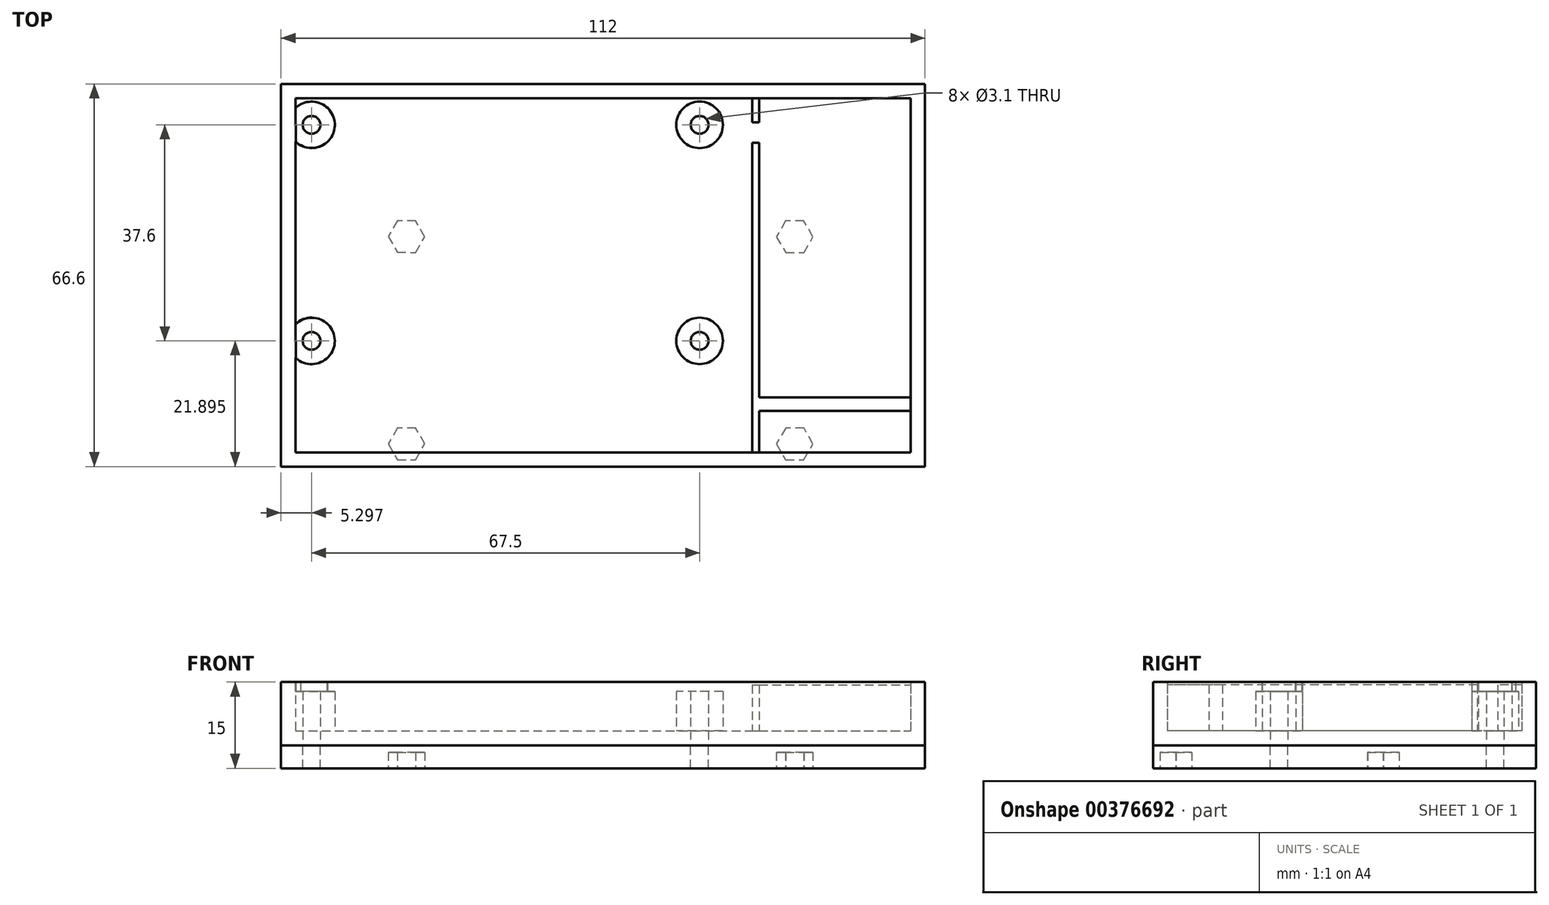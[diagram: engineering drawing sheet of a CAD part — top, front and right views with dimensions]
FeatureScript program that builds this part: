
annotation { "Feature Type Name" : "Feature", "Feature Type Description" : "" }
export const myFeature = defineFeature(function(context is Context, id is Id, definition is map)
    precondition{}
    {
        {
            var Q0;
            Q0=qCreatedBy(makeId("Top.planeOp"),FACE);
            var sketch = newSketch(context, id + "F0", { "sketchPlane" : qUnion([Q0])});
            skLineSegment(sketch, "E0.bottom", {"start": v(-67.04, 57.24) * mm, "end": v(44.96, 57.24) * mm});
            skLineSegment(sketch, "E0.top", {"start": v(-67.04, -9.36) * mm, "end": v(-25.04, -9.36) * mm});
            skLineSegment(sketch, "E0.left", {"start": v(-67.04, 57.24) * mm, "end": v(-67.04, -9.36) * mm});
            skLineSegment(sketch, "E0.right", {"start": v(44.96, 57.24) * mm, "end": v(44.96, -9.36) * mm});
            skLineSegment(sketch, "E1", {"start": v(44.63, 50.14) * mm, "end": v(176.63, 50.14) * mm, "construction": true});
            skLineSegment(sketch, "E2", {"start": v(42, 12.54) * mm, "end": v(176.63, 12.54) * mm, "construction": true});
            skLineSegment(sketch, "E3", {"start": v(-61.74, -1.53) * mm, "end": v(-61.74, -83.47) * mm, "construction": true});
            skLineSegment(sketch, "E4", {"start": v(5.76, -0.22) * mm, "end": v(5.76, -80.28) * mm, "construction": true});
            skLineSegment(sketch, "E5", {"start": v(1.1, -53.47) * mm, "end": v(1.1, -86.28) * mm, "construction": true});
            skLineSegment(sketch, "E6", {"start": v(38.82, -0.26) * mm, "end": v(130.32, -0.26) * mm, "construction": true});
            skCircle(sketch, "E7", {"center": v(-61.74, 50.14) * mm, "radius": 1.55 * mm});
            skCircle(sketch, "E8", {"center": v(5.76, 50.14) * mm, "radius": 1.55 * mm});
            skCircle(sketch, "E9", {"center": v(-61.74, 12.54) * mm, "radius": 1.55 * mm});
            skCircle(sketch, "E10", {"center": v(5.76, 12.54) * mm, "radius": 1.55 * mm});
            skLineSegment(sketch, "E11", {"start": v(-13.54, -55.9) * mm, "end": v(-13.54, -82.43) * mm, "construction": true});
            skLineSegment(sketch, "E12.trimOffspring", {"start": v(-13.54, -9.36) * mm, "end": v(44.96, -9.36) * mm});
            skLineSegment(sketch, "E13", {"start": v(-25.04, -9.36) * mm, "end": v(-13.54, -9.36) * mm});
            skSolve(sketch);
        }
        {
            var Q0;
            Q0 = qSketchRegion(id + "F0", true);
            var Q1;
            {var subQ0=sQuery(id+"F0.wireOp",EDGE,"FsC10DJD-oyt9-5rBi-kH7v-Q8Pfx3An0YuG");Q1=makeQuery(id+"F0.imprint","IMPRINT",FACE,{"disambiguationData":[TD([[makeQuery(id+"F0.imprint","IMPRINT",EDGE,{"derivedFrom":subQ0}),-1.0]])]});}
            extrude(context, id + "F1", {"entities" : qUnion([Q0, Q1]), "oppositeDirection" : true, "depth" : 4 * mm});
        }
        {
            var Q0;
            Q0=makeQuery(id+"F0.imprint","IMPRINT",FACE,{"disambiguationData":[TD([[makeQuery(id+"F0.imprint","IMPRINT",EDGE,{"derivedFrom":sQuery(id+"F0.wireOp",EDGE,"E0.bottom")}),-1.0]])]});
            extrude(context, id + "F2", {"entities" : qUnion([Q0]), "depth" : 11 * mm});
        }
        {
            var Q0;
            Q0=makeQuery(id+"F2.opExtrude","CAP_FACE",FACE,{"disambiguationData":[OSD([sQuery(id+"F0.wireOp",EDGE,"E0.bottom"),sQuery(id+"F0.wireOp",EDGE,"E0.top"),sQuery(id+"F0.wireOp",EDGE,"E0.left"),sQuery(id+"F0.wireOp",EDGE,"E0.right"),sQuery(id+"F0.wireOp",EDGE,"E7"),sQuery(id+"F0.wireOp",EDGE,"E8"),sQuery(id+"F0.wireOp",EDGE,"E9"),sQuery(id+"F0.wireOp",EDGE,"E10"),sQuery(id+"F0.wireOp",EDGE,"E12.trimOffspring"),sQuery(id+"F0.wireOp",EDGE,"E13")])],"isStart":false});
            shell(context, id + "F3", {"entities" : qUnion([Q0]), "thickness" : 2.5 * mm});
        }
        {
            var Q0;
            {var subQ0=sQuery(id+"F0.wireOp",EDGE,"E13");var subQ1=sQuery(id+"F0.wireOp",EDGE,"E12.trimOffspring");var subQ2=sQuery(id+"F0.wireOp",EDGE,"E10");var subQ3=sQuery(id+"F0.wireOp",EDGE,"E9");var subQ4=sQuery(id+"F0.wireOp",EDGE,"E8");var subQ5=sQuery(id+"F0.wireOp",EDGE,"E7");var subQ6=sQuery(id+"F0.wireOp",EDGE,"E0.right");var subQ7=sQuery(id+"F0.wireOp",EDGE,"E0.left");var subQ8=sQuery(id+"F0.wireOp",EDGE,"E0.top");var subQ9=sQuery(id+"F0.wireOp",EDGE,"E0.bottom");Q0=makeQuery(id+"F3.opShell","OFFSET_FACE",FACE,{"disambiguationData":[OSD([subQ9,subQ8,subQ7,subQ6,subQ5,subQ4,subQ3,subQ2,subQ1,subQ0]),TDD([makeQuery(id+"F2.opExtrude","CAP_FACE",FACE,{"disambiguationData":[OSD([subQ9,subQ8,subQ7,subQ6,subQ5,subQ4,subQ3,subQ2,subQ1,subQ0])],"isStart":true})])]});}
            cPlane(context, id + "F4", {"entities" : qUnion([Q0]), "cplaneType" : CPlaneType.OFFSET, "offset" : 0 * mm, "width" : 150 * mm, "height" : 150 * mm});
        }
        {
            var Q0;
            Q0=qCreatedBy(id+"F4.planeOp",FACE);
            var sketch = newSketch(context, id + "F5", { "sketchPlane" : qUnion([Q0])});
            skLineSegment(sketch, "E14.bottom", {"start": v(14.9, 54.77) * mm, "end": v(16.11, 54.77) * mm});
            skLineSegment(sketch, "E14.top", {"start": v(14.9, 50.6) * mm, "end": v(16.11, 50.6) * mm});
            skLineSegment(sketch, "E14.left", {"start": v(14.9, 54.77) * mm, "end": v(14.9, 50.6) * mm});
            skLineSegment(sketch, "E14.right", {"start": v(16.11, 54.77) * mm, "end": v(16.11, 50.6) * mm});
            skLineSegment(sketch, "E15.bottom", {"start": v(14.92, 47.04) * mm, "end": v(16.11, 47.04) * mm});
            skLineSegment(sketch, "E15.top", {"start": v(14.92, -6.86) * mm, "end": v(16.11, -6.86) * mm});
            skLineSegment(sketch, "E15.left", {"start": v(14.92, 47.04) * mm, "end": v(14.92, -6.86) * mm});
            skLineSegment(sketch, "E15.right", {"start": v(16.11, 47.04) * mm, "end": v(16.11, -6.86) * mm});
            skLineSegment(sketch, "E16.bottom", {"start": v(16.11, 2.7) * mm, "end": v(42.48, 2.7) * mm});
            skLineSegment(sketch, "E16.top", {"start": v(16.11, 0.35) * mm, "end": v(42.48, 0.35) * mm});
            skLineSegment(sketch, "E16.left", {"start": v(16.11, 2.7) * mm, "end": v(16.11, 0.35) * mm});
            skLineSegment(sketch, "E16.right", {"start": v(42.48, 2.7) * mm, "end": v(42.48, 0.35) * mm});
            skSolve(sketch);
        }
        {
            var Q0;
            Q0=makeQuery(id+"F5.imprint","IMPRINT",FACE,{"disambiguationData":[TD([[makeQuery(id+"F5.imprint","IMPRINT",EDGE,{"derivedFrom":sQuery(id+"F5.wireOp",EDGE,"E14.bottom")}),-1.0]])]});
            var Q1;
            {var subQ1=sQuery(id+"F5.wireOp",EDGE,"E15.bottom");Q1=makeQuery(id+"F5.imprint","IMPRINT",FACE,{"disambiguationData":[TD([[makeQuery(id+"F5.imprint","IMPRINT",EDGE,{"derivedFrom":subQ1}),-1.0]])]});}
            var Q2;
            Q2=makeQuery(id+"F5.imprint","IMPRINT",FACE,{"disambiguationData":[TD([[makeQuery(id+"F5.imprint","IMPRINT",EDGE,{"derivedFrom":sQuery(id+"F5.wireOp",EDGE,"E16.bottom")}),-1.0]])]});
            extrude(context, id + "F6", {"entities" : qUnion([Q0, Q1, Q2]), "depth" : 8 * mm});
        }
        {
            var Q0;
            Q0=makeQuery(id+"F2.opExtrude","CAP_FACE",FACE,{"disambiguationData":[OSD([sQuery(id+"F0.wireOp",EDGE,"A0NuOWqy-mbow-oFeQ-aFUs-JcpJWNl4cWgZ.bottom"),sQuery(id+"F0.wireOp",EDGE,"A0NuOWqy-mbow-oFeQ-aFUs-JcpJWNl4cWgZ.top"),sQuery(id+"F0.wireOp",EDGE,"A0NuOWqy-mbow-oFeQ-aFUs-JcpJWNl4cWgZ.left"),sQuery(id+"F0.wireOp",EDGE,"A0NuOWqy-mbow-oFeQ-aFUs-JcpJWNl4cWgZ.right"),sQuery(id+"F0.wireOp",EDGE,"l8DgdMRk-jwTu-yn87-Ubay-0boQf5sXXbED"),sQuery(id+"F0.wireOp",EDGE,"IFopZNKl-To2k-V7rv-e193-DWKehgoEgPML"),sQuery(id+"F0.wireOp",EDGE,"wSwp0tQP-pvOi-1nlV-F12w-8n0LTa4ZxAE6"),sQuery(id+"F0.wireOp",EDGE,"Evtd0GlZ-4YtB-NOmt-JUBp-SgV2YzHuL3n0"),sQuery(id+"F0.wireOp",EDGE,"269334cf-922f-445a-855f-7391bd0f7049.trimOffspring"),sQuery(id+"F0.wireOp",EDGE,"TvPx72jC-Pm7q-U3J5-DLNJ-bXEKM7csz5V9"),sQuery(id+"F0.wireOp",EDGE,"zx5NMsNx-JtPk-FpRE-2ajY-Q3JxvkHSanLY"),sQuery(id+"F0.wireOp",EDGE,"5lGAd6N5-jAS0-xnDL-4Krg-xO5UTL4uwT4z"),sQuery(id+"F0.wireOp",EDGE,"S9dVnHw2-FrOM-Ck64-E3qb-46jiesPe1zGM")])],"isStart":false});
            var Q1;
            {var subQ0=sQuery(id+"F0.wireOp",EDGE,"E13");var subQ1=sQuery(id+"F0.wireOp",EDGE,"E12.trimOffspring");var subQ2=sQuery(id+"F0.wireOp",EDGE,"E10");var subQ3=sQuery(id+"F0.wireOp",EDGE,"E9");var subQ4=sQuery(id+"F0.wireOp",EDGE,"E8");var subQ5=sQuery(id+"F0.wireOp",EDGE,"E7");var subQ6=sQuery(id+"F0.wireOp",EDGE,"E0.right");var subQ7=sQuery(id+"F0.wireOp",EDGE,"E0.left");var subQ8=sQuery(id+"F0.wireOp",EDGE,"E0.top");var subQ9=sQuery(id+"F0.wireOp",EDGE,"E0.bottom");Q1=makeQuery(id+"F3.opShell","OFFSET_FACE",FACE,{"disambiguationData":[OSD([subQ9,subQ8,subQ7,subQ6,subQ5,subQ4,subQ3,subQ2,subQ1,subQ0]),TDD([makeQuery(id+"F2.opExtrude","CAP_FACE",FACE,{"disambiguationData":[OSD([subQ9,subQ8,subQ7,subQ6,subQ5,subQ4,subQ3,subQ2,subQ1,subQ0])],"isStart":false})]),OD(1.0)]});}
            cPlane(context, id + "F7", {"entities" : qUnion([Q0, Q1]), "cplaneType" : CPlaneType.OFFSET, "offset" : 0 * mm, "width" : 150 * mm, "height" : 150 * mm});
        }
        {
            var Q0;
            Q0=qCreatedBy(id+"F7.planeOp",FACE);
            var sketch = newSketch(context, id + "F8", { "sketchPlane" : qUnion([Q0])});
            skArc(sketch, "E17", {"start": v(-64.48, 47.2) * mm, "mid": v(-57.67, 50.2) * mm, "end": v(-64.53, 53.06) * mm});
            skLineSegment(sketch, "E18", {"start": v(-64.53, 53.06) * mm, "end": v(-64.48, 47.2) * mm});
            skArc(sketch, "E19", {"start": v(-64.48, 9.53) * mm, "mid": v(-57.66, 12.55) * mm, "end": v(-64.55, 15.4) * mm});
            skLineSegment(sketch, "E20", {"start": v(-64.55, 15.4) * mm, "end": v(-64.48, 9.53) * mm});
            skCircle(sketch, "E21", {"center": v(5.75, 50.14) * mm, "radius": 4.24 * mm});
            skCircle(sketch, "E22", {"center": v(5.75, 12.54) * mm, "radius": 4.31 * mm});
            skSolve(sketch);
        }
        {
            var Q0;
            Q0=makeQuery(id+"F8.imprint","IMPRINT",FACE,{"disambiguationData":[TD([[makeQuery(id+"F8.imprint","IMPRINT",EDGE,{"derivedFrom":sQuery(id+"F8.wireOp",EDGE,"E21")}),1.0]])]});
            var Q1;
            Q1=makeQuery(id+"F8.imprint","IMPRINT",FACE,{"disambiguationData":[TD([[makeQuery(id+"F8.imprint","IMPRINT",EDGE,{"derivedFrom":sQuery(id+"F8.wireOp",EDGE,"E22")}),1.0]])]});
            var Q2;
            Q2=makeQuery(id+"F8.imprint","IMPRINT",FACE,{"disambiguationData":[TD([[makeQuery(id+"F8.imprint","IMPRINT",EDGE,{"derivedFrom":sQuery(id+"F8.wireOp",EDGE,"E17")}),1.0]])]});
            var Q3;
            Q3=makeQuery(id+"F8.imprint","IMPRINT",FACE,{"disambiguationData":[TD([[makeQuery(id+"F8.imprint","IMPRINT",EDGE,{"derivedFrom":sQuery(id+"F8.wireOp",EDGE,"E19")}),1.0]])]});
            extrude(context, id + "F9", {"entities" : qUnion([Q0, Q1, Q2, Q3]), "operationType" : NewBodyOperationType.REMOVE, "oppositeDirection" : true, "depth" : 1.62 * mm});
        }
        {
            var Q0;
            Q0=makeQuery(id+"F1.opExtrude","CAP_FACE",FACE,{"disambiguationData":[OSD([sQuery(id+"F0.wireOp",EDGE,"E0.bottom"),sQuery(id+"F0.wireOp",EDGE,"E0.top"),sQuery(id+"F0.wireOp",EDGE,"E0.left"),sQuery(id+"F0.wireOp",EDGE,"E0.right"),sQuery(id+"F0.wireOp",EDGE,"E7"),sQuery(id+"F0.wireOp",EDGE,"E8"),sQuery(id+"F0.wireOp",EDGE,"E9"),sQuery(id+"F0.wireOp",EDGE,"E10"),sQuery(id+"F0.wireOp",EDGE,"E12.trimOffspring"),sQuery(id+"F0.wireOp",EDGE,"E13")])],"isStart":false});
            cPlane(context, id + "F10", {"entities" : qUnion([Q0]), "cplaneType" : CPlaneType.OFFSET, "offset" : 0 * mm, "width" : 150 * mm, "height" : 150 * mm});
        }
        {
            var Q0;
            Q0=qCreatedBy(id+"F10.planeOp",FACE);
            var sketch = newSketch(context, id + "F11", { "sketchPlane" : qUnion([Q0])});
            skCircle(sketch, "E23.cCircle", {"center": v(-45.2, 5.39) * mm, "radius": 2.75 * mm, "construction": true});
            skLineSegment(sketch, "E23.0", {"start": v(-42.03, 5.4) * mm, "end": v(-43.61, 2.65) * mm});
            skLineSegment(sketch, "E23.1", {"start": v(-43.61, 2.65) * mm, "end": v(-46.79, 2.63) * mm});
            skLineSegment(sketch, "E23.2", {"start": v(-46.79, 2.63) * mm, "end": v(-48.39, 5.38) * mm});
            skLineSegment(sketch, "E23.3", {"start": v(-48.39, 5.38) * mm, "end": v(-46.8, 8.13) * mm});
            skLineSegment(sketch, "E23.4", {"start": v(-46.8, 8.13) * mm, "end": v(-43.63, 8.15) * mm});
            skLineSegment(sketch, "E23.5", {"start": v(-43.63, 8.15) * mm, "end": v(-42.03, 5.4) * mm});
            skPoint(sketch, "E23.0.midPoint", {"position": v(-42.82, 4.02) * mm});
            skCircle(sketch, "E24.cCircle", {"center": v(-45.23, -30.69) * mm, "radius": 2.75 * mm, "construction": true});
            skLineSegment(sketch, "E24.0", {"start": v(-48.4, -30.71) * mm, "end": v(-46.84, -27.95) * mm});
            skLineSegment(sketch, "E24.1", {"start": v(-46.84, -27.95) * mm, "end": v(-43.66, -27.92) * mm});
            skLineSegment(sketch, "E24.2", {"start": v(-43.66, -27.92) * mm, "end": v(-42.05, -30.66) * mm});
            skLineSegment(sketch, "E24.3", {"start": v(-42.05, -30.66) * mm, "end": v(-43.62, -33.42) * mm});
            skLineSegment(sketch, "E24.4", {"start": v(-43.62, -33.42) * mm, "end": v(-46.8, -33.45) * mm});
            skLineSegment(sketch, "E24.5", {"start": v(-46.8, -33.45) * mm, "end": v(-48.4, -30.71) * mm});
            skPoint(sketch, "E24.0.midPoint", {"position": v(-47.62, -29.33) * mm});
            skCircle(sketch, "E25.cCircle", {"center": v(22.3, 5.4) * mm, "radius": 2.75 * mm, "construction": true});
            skLineSegment(sketch, "E25.0", {"start": v(20.72, 2.65) * mm, "end": v(19.13, 5.4) * mm});
            skLineSegment(sketch, "E25.1", {"start": v(19.13, 5.4) * mm, "end": v(20.7, 8.15) * mm});
            skLineSegment(sketch, "E25.2", {"start": v(20.7, 8.15) * mm, "end": v(23.88, 8.15) * mm});
            skLineSegment(sketch, "E25.3", {"start": v(23.88, 8.15) * mm, "end": v(25.48, 5.4) * mm});
            skLineSegment(sketch, "E25.4", {"start": v(25.48, 5.4) * mm, "end": v(23.9, 2.65) * mm});
            skLineSegment(sketch, "E25.5", {"start": v(23.9, 2.65) * mm, "end": v(20.72, 2.65) * mm});
            skPoint(sketch, "E25.0.midPoint", {"position": v(19.92, 4.02) * mm});
            skCircle(sketch, "E26.cCircle", {"center": v(22.3, -30.65) * mm, "radius": 2.75 * mm, "construction": true});
            skLineSegment(sketch, "E26.0", {"start": v(19.13, -30.64) * mm, "end": v(20.72, -27.9) * mm});
            skLineSegment(sketch, "E26.1", {"start": v(20.72, -27.9) * mm, "end": v(23.9, -27.9) * mm});
            skLineSegment(sketch, "E26.2", {"start": v(23.9, -27.9) * mm, "end": v(25.48, -30.66) * mm});
            skLineSegment(sketch, "E26.3", {"start": v(25.48, -30.66) * mm, "end": v(23.89, -33.4) * mm});
            skLineSegment(sketch, "E26.4", {"start": v(23.89, -33.4) * mm, "end": v(20.71, -33.4) * mm});
            skLineSegment(sketch, "E26.5", {"start": v(20.71, -33.4) * mm, "end": v(19.13, -30.64) * mm});
            skPoint(sketch, "E26.0.midPoint", {"position": v(19.92, -29.27) * mm});
            skSolve(sketch);
        }
        {
            var Q0;
            Q0 = qSketchRegion(id + "F11", true);
            extrude(context, id + "F12", {"entities" : qUnion([Q0]), "operationType" : NewBodyOperationType.REMOVE, "oppositeDirection" : true, "depth" : 2.8 * mm});
        }
    });
